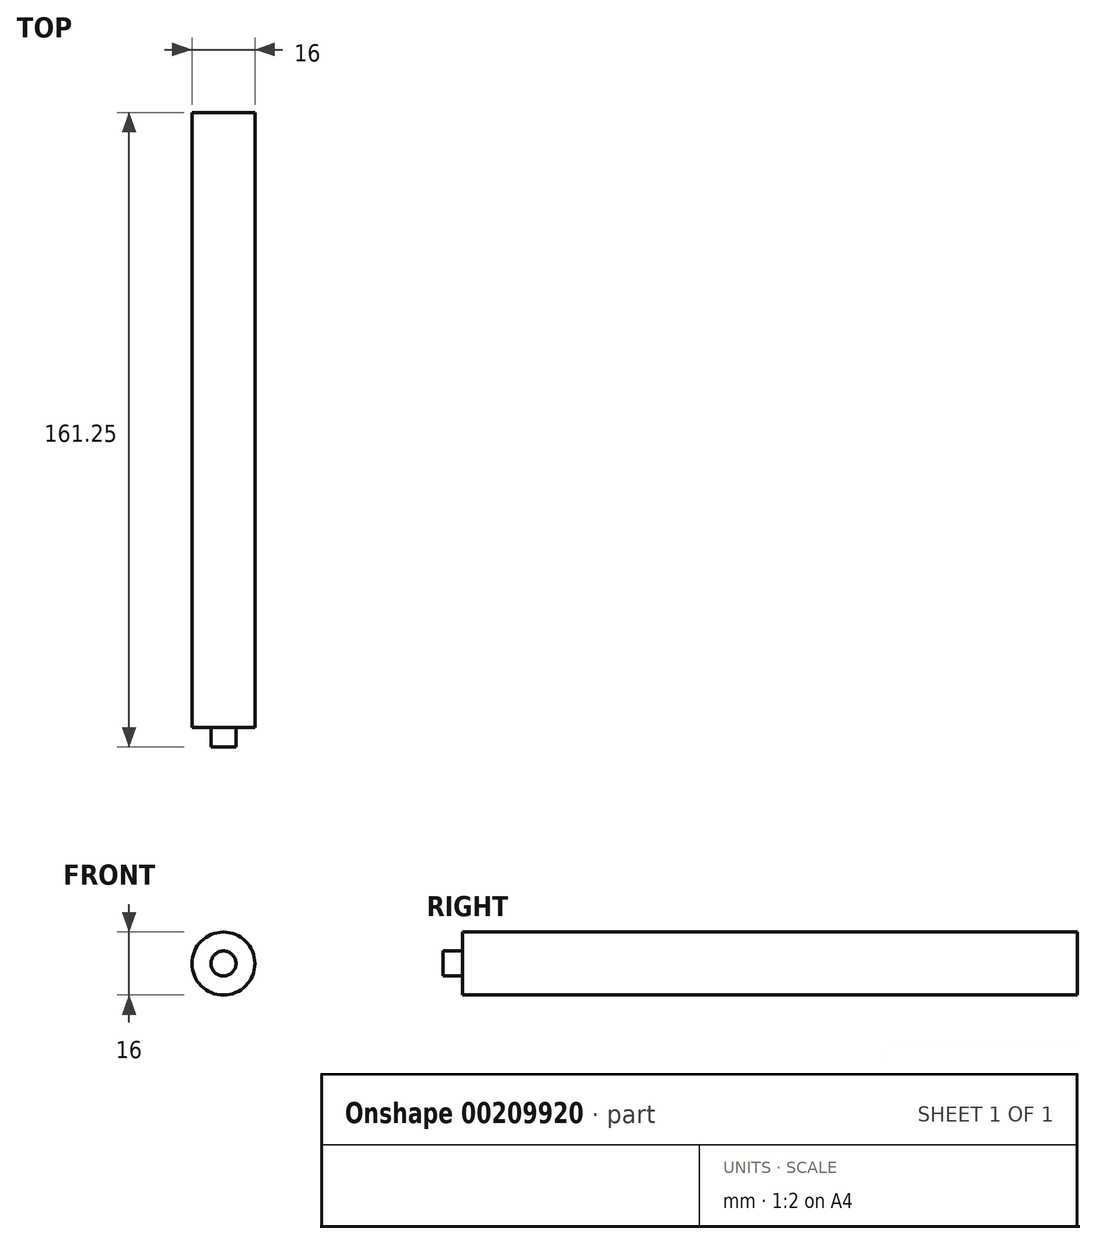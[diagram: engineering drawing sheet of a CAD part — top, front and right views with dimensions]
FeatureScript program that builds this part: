
annotation { "Feature Type Name" : "Feature", "Feature Type Description" : "" }
export const myFeature = defineFeature(function(context is Context, id is Id, definition is map)
    precondition{}
    {
        {
            var Q0;
            Q0=qCreatedBy(makeId("Front.planeOp"),FACE);
            var sketch = newSketch(context, id + "F0", { "sketchPlane" : qUnion([Q0])});
            skCircle(sketch, "E0", {"center": v(0, 0) * mm, "radius": 8 * mm});
            skSolve(sketch);
        }
        {
            var Q0;
            Q0 = qSketchRegion(id + "F0", true);
            extrude(context, id + "F1", {"entities" : qUnion([Q0]), "depth" : 156.25 * mm});
        }
        {
            var Q0;
            Q0=makeQuery(id+"F1.opExtrude","CAP_FACE",FACE,{"disambiguationData":[OSD([sQuery(id+"F0.wireOp",EDGE,"E0")])],"isStart":false});
            var sketch = newSketch(context, id + "F2", { "sketchPlane" : qUnion([Q0])});
            skCircle(sketch, "E1", {"center": v(0, 0) * mm, "radius": 3.18 * mm});
            skSolve(sketch);
        }
        {
            var Q0;
            Q0 = qSketchRegion(id + "F2", true);
            extrude(context, id + "F3", {"entities" : qUnion([Q0]), "depth" : 5 * mm});
        }
        {
            var Q0;
            Q0=qCreatedBy(makeId("Front.planeOp"),FACE);
            cPlane(context, id + "F4", {"entities" : qUnion([Q0]), "cplaneType" : CPlaneType.OFFSET, "offset" : 78.12 * mm, "width" : 150 * mm, "height" : 150 * mm});
        }
    });
